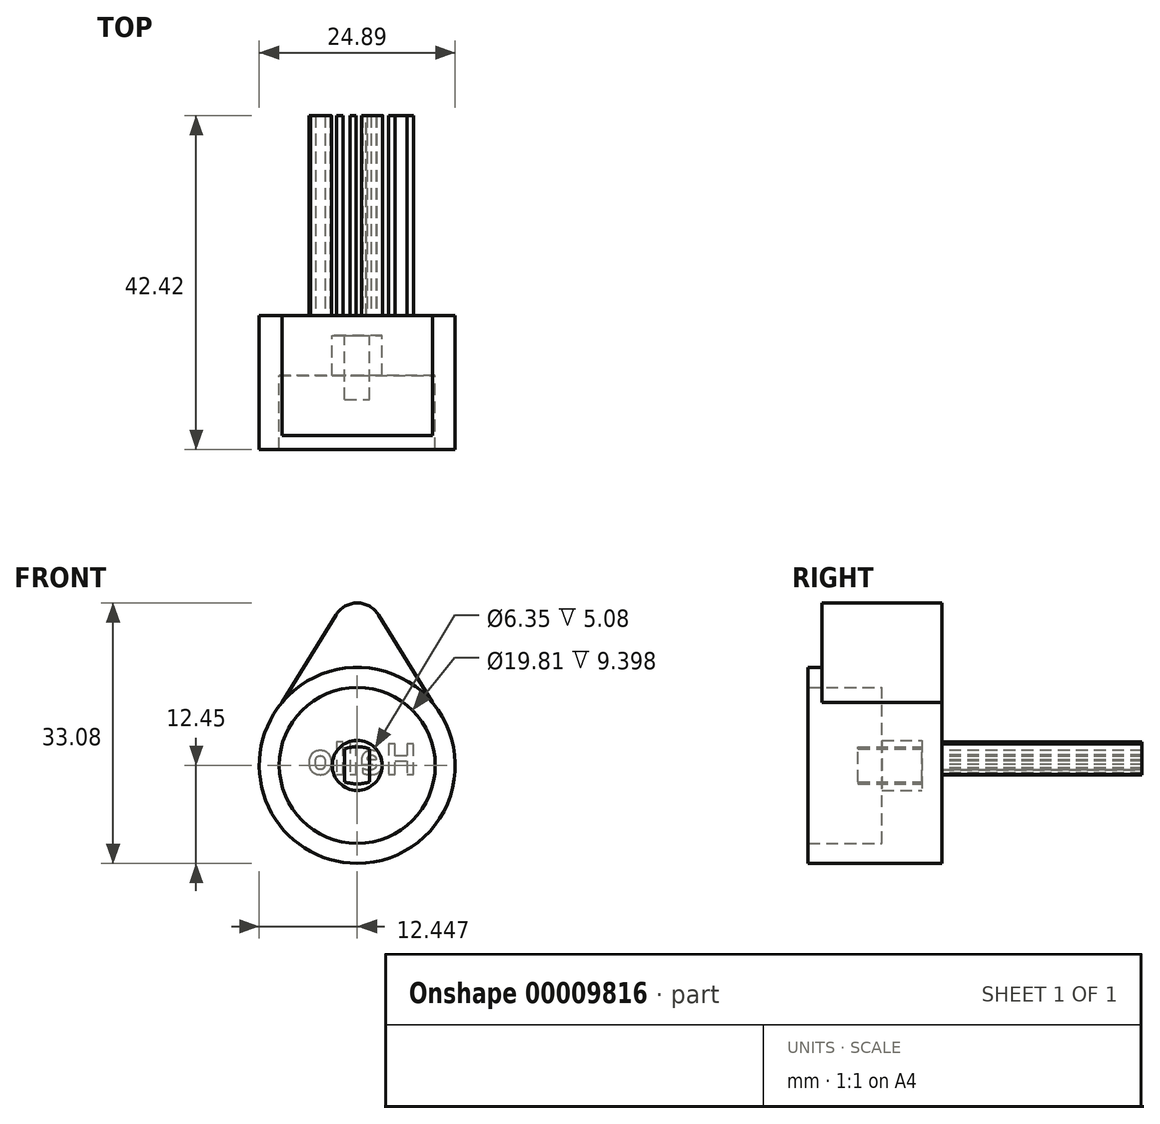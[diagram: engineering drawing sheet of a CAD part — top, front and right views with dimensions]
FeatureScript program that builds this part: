
annotation { "Feature Type Name" : "Feature", "Feature Type Description" : "" }
export const myFeature = defineFeature(function(context is Context, id is Id, definition is map)
    precondition{}
    {
        {
            var Q0;
            Q0=qCreatedBy(makeId("Front.planeOp"),FACE);
            var sketch = newSketch(context, id + "F0", { "sketchPlane" : qUnion([Q0])});
            skArc(sketch, "E0.0.MirrorCS", {"start": v(3.18, 0.25) * mm, "mid": v(1.59, 0) * mm, "end": v(0, 0.25) * mm});
            skLineSegment(sketch, "E1", {"start": v(0, 0.25) * mm, "end": v(0, 4.45) * mm});
            skLineSegment(sketch, "E2", {"start": v(3.18, 0.25) * mm, "end": v(3.18, 4.45) * mm});
            skArc(sketch, "E3.0.MirrorCS", {"start": v(3.18, 4.45) * mm, "mid": v(1.59, 4.7) * mm, "end": v(0, 4.45) * mm});
            skCircle(sketch, "E4", {"center": v(1.59, 2.35) * mm, "radius": 12.45 * mm});
            skPoint(sketch, "E5.0.MirrorCS.end.orphan", {"position": v(1.59, 4.45) * mm});
            skPoint(sketch, "E6.orphan", {"position": v(1.59, 4.7) * mm});
            skPoint(sketch, "E7.orphan", {"position": v(0, 2.35) * mm});
            skPoint(sketch, "E8.end.orphan", {"position": v(3.17, 2.35) * mm});
            skPoint(sketch, "E9.end.orphan", {"position": v(1.59, 0) * mm});
            skPoint(sketch, "E9.start.orphan", {"position": v(1.59, 0.25) * mm});
            skLineSegment(sketch, "E10.0", {"start": v(-2.54, -1.33) * mm, "end": v(-2.54, 6.03) * mm});
            skArc(sketch, "E10.1", {"start": v(5.72, -1.33) * mm, "mid": v(1.59, -2.54) * mm, "end": v(-2.54, -1.33) * mm});
            skLineSegment(sketch, "E10.2", {"start": v(5.72, -1.33) * mm, "end": v(5.72, 6.03) * mm});
            skArc(sketch, "E10.3", {"start": v(5.72, 6.03) * mm, "mid": v(1.59, 7.24) * mm, "end": v(-2.54, 6.03) * mm});
            skCircle(sketch, "E11", {"center": v(1.59, 2.35) * mm, "radius": 9.9 * mm});
            skSolve(sketch);
        }
        {
            var Q0;
            Q0=makeQuery(id+"F0.imprint","IMPRINT",FACE,{"disambiguationData":[TD([[makeQuery(id+"F0.imprint","IMPRINT",EDGE,{"derivedFrom":sQuery(id+"F0.wireOp",EDGE,"E4")}),1.0]])]});
            var Q1;
            Q1=makeQuery(id+"F0.imprint","IMPRINT",FACE,{"disambiguationData":[TD([[makeQuery(id+"F0.imprint","IMPRINT",EDGE,{"derivedFrom":sQuery(id+"F0.wireOp",EDGE,"E0.0.MirrorCS")}),1.0]])]});
            extrude(context, id + "F1", {"entities" : qUnion([Q0, Q1]), "depth" : 8.13 * mm});
        }
        {
            var Q0;
            Q0=makeQuery(id+"F1.opExtrude","CAP_FACE",FACE,{"disambiguationData":[OSD([sQuery(id+"F0.wireOp",EDGE,"E4"),sQuery(id+"F0.wireOp",EDGE,"E11")])],"isStart":false});
            var sketch = newSketch(context, id + "F2", { "sketchPlane" : qUnion([Q0])});
            skCircle(sketch, "E12", {"center": v(1.59, 2.35) * mm, "radius": 9.9 * mm});
            skCircle(sketch, "E13", {"center": v(1.59, 2.35) * mm, "radius": 12.45 * mm});
            skSolve(sketch);
        }
        {
            var Q0;
            Q0=makeQuery(id+"F2.imprint","IMPRINT",FACE,{"disambiguationData":[TD([[makeQuery(id+"F2.imprint","IMPRINT",EDGE,{"derivedFrom":sQuery(id+"F2.wireOp",EDGE,"E12")}),-1.0]])]});
            extrude(context, id + "F3", {"entities" : qUnion([Q0]), "depth" : 6.35 * mm});
        }
        {
            var Q0;
            Q0=makeQuery(id+"F1.opExtrude","CAP_FACE",FACE,{"disambiguationData":[OSD([sQuery(id+"F0.wireOp",EDGE,"E4"),sQuery(id+"F0.wireOp",EDGE,"E11")])],"isStart":true});
            var sketch = newSketch(context, id + "F4", { "sketchPlane" : qUnion([Q0])});
            skCircle(sketch, "E14", {"center": v(-1.59, 2.35) * mm, "radius": 9.9 * mm});
            skCircle(sketch, "E15", {"center": v(-1.59, 2.35) * mm, "radius": 3.18 * mm});
            skSolve(sketch);
        }
        {
            var Q0;
            Q0 = qSketchRegion(id + "F4", true);
            extrude(context, id + "F5", {"entities" : qUnion([Q0]), "oppositeDirection" : true, "depth" : 5.08 * mm});
        }
        {
            var Q0;
            Q0=makeQuery(id+"F1.opExtrude","CAP_FACE",FACE,{"disambiguationData":[OSD([sQuery(id+"F0.wireOp",EDGE,"E4"),sQuery(id+"F0.wireOp",EDGE,"E11")])],"isStart":true});
            var sketch = newSketch(context, id + "F6", { "sketchPlane" : qUnion([Q0])});
            skCircle(sketch, "E16", {"center": v(-1.59, 2.35) * mm, "radius": 12.45 * mm});
            skSolve(sketch);
        }
        {
            var Q0;
            Q0 = qSketchRegion(id + "F6", true);
            extrude(context, id + "F7", {"entities" : qUnion([Q0]), "depth" : 2.54 * mm});
        }
        {
            var Q0;
            Q0=makeQuery(id+"F7.opExtrude","CAP_FACE",FACE,{"disambiguationData":[OSD([sQuery(id+"F6.wireOp",EDGE,"E16")])],"isStart":false});
            var sketch = newSketch(context, id + "F8", { "sketchPlane" : qUnion([Q0])});
            skLineSegment(sketch, "E17", {"start": v(-13.02, 7.27) * mm, "end": v(-4.3, 21.46) * mm});
            skLineSegment(sketch, "E18", {"start": v(1.12, 21.46) * mm, "end": v(9.84, 7.27) * mm});
            skLineSegment(sketch, "E19", {"start": v(9.84, 7.27) * mm, "end": v(3.5, 7.27) * mm});
            skLineSegment(sketch, "E20", {"start": v(-1.59, 7.27) * mm, "end": v(-1.59, 2.35) * mm});
            skLineSegment(sketch, "E21", {"start": v(-1.59, 7.27) * mm, "end": v(-1.59, 12.35) * mm});
            skPoint(sketch, "E22.visualSharp", {"position": v(-1.59, 25.86) * mm});
            skArc(sketch, "E22.filletArc", {"start": v(1.12, 21.46) * mm, "mid": v(-1.59, 22.98) * mm, "end": v(-4.3, 21.46) * mm});
            skArc(sketch, "E23", {"start": v(3.5, 7.27) * mm, "mid": v(-1.59, 12.35) * mm, "end": v(-6.67, 7.27) * mm});
            skLineSegment(sketch, "E24.trimOffspring", {"start": v(-6.67, 7.27) * mm, "end": v(-13.02, 7.27) * mm});
            skLineSegment(sketch, "E25.trimOffspring", {"start": v(-1.59, 22.98) * mm, "end": v(-1.59, 25.86) * mm});
            skSolve(sketch);
        }
        {
            var Q0;
            Q0 = qSketchRegion(id + "F8", true);
            extrude(context, id + "F9", {"entities" : qUnion([Q0]), "operationType" : NewBodyOperationType.ADD, "oppositeDirection" : true, "depth" : 15.24 * mm});
        }
        {
            var Q0;
            Q0=makeQuery(id+"F3.opExtrude","CAP_FACE",FACE,{"disambiguationData":[OSD([sQuery(id+"F2.wireOp",EDGE,"E12"),sQuery(id+"F2.wireOp",EDGE,"E13")])],"isStart":false});
            var sketch = newSketch(context, id + "F10", { "sketchPlane" : qUnion([Q0])});
            skSolve(sketch);
        }
        {
            var Q0;
            Q0=makeQuery(id+"F10.imprint","IMPRINT",FACE,{"disambiguationData":[TD([[makeQuery(id+"F10.imprint","IMPRINT",EDGE,{"derivedFrom":makeQuery(id+"F3.opExtrude","CAP_EDGE",EDGE,{"disambiguationData":[OSD([sQuery(id+"F2.wireOp",EDGE,"E12")])],"isStart":false})}),-1.0]])]});
            var sketch = newSketch(context, id + "F11", { "sketchPlane" : qUnion([Q0])});
            skCircle(sketch, "E26", {"center": v(1.59, 2.35) * mm, "radius": 9.9 * mm});
            skCircle(sketch, "E27", {"center": v(1.59, 2.35) * mm, "radius": 6.57 * mm});
            skSolve(sketch);
        }
        {
            var Q0;
            Q0 = qSketchRegion(id + "F11", true);
            var Q1;
            Q1=makeQuery(id+"F5.opExtrude","CAP_FACE",FACE,{"disambiguationData":[OSD([sQuery(id+"F4.wireOp",EDGE,"E14"),sQuery(id+"F4.wireOp",EDGE,"E15")])],"isStart":false});
            extrude(context, id + "F12", {"entities" : qUnion([Q0]), "operationType" : NewBodyOperationType.REMOVE, "endBound" : BoundingType.UP_TO_SURFACE, "oppositeDirection" : true, "endBoundEntityFace" : qUnion([Q1]), "depth" : 25.4 * mm});
        }
        {
            var Q0;
            Q0=makeQuery(id+"F9.boolean.opBoolean","MERGE",FACE,{"derivedFrom":[makeQuery(id+"F7.opExtrude","CAP_FACE",FACE,{"disambiguationData":[OSD([sQuery(id+"F6.wireOp",EDGE,"E16")])],"isStart":false}),makeQuery(id+"F9.opExtrude","CAP_FACE",FACE,{"disambiguationData":[OSD([sQuery(id+"F8.wireOp",EDGE,"E17"),sQuery(id+"F8.wireOp",EDGE,"E18"),sQuery(id+"F8.wireOp",EDGE,"E19"),sQuery(id+"F8.wireOp",EDGE,"E22.filletArc"),sQuery(id+"F8.wireOp",EDGE,"E23"),sQuery(id+"F8.wireOp",EDGE,"E24.trimOffspring")])],"isStart":true})]});
            var sketch = newSketch(context, id + "F13", { "sketchPlane" : qUnion([Q0])});
            skText(sketch, "E28", { "text": "Hello", "fontName": "OpenSans-Bold.ttf"});
            const initialGuessF13  = {"E28": [-0.00922, 0.00122, 1, 0, 0.0039]};
            skSetInitialGuess(sketch, initialGuessF13);
            skSolve(sketch);
        }
        {
            var Q0;
            Q0=makeQuery(id+"F13.imprint","IMPRINT",FACE,{"disambiguationData":[TD([[makeQuery(id+"F13.imprint","IMPRINT",EDGE,{"derivedFrom":sQuery(id+"F13.wireOp",EDGE,"E28.sketch_text.stroke-32")}),-1.0]])]});
            var Q1;
            Q1=makeQuery(id+"F13.imprint","IMPRINT",FACE,{"disambiguationData":[TD([[makeQuery(id+"F13.imprint","IMPRINT",EDGE,{"derivedFrom":sQuery(id+"F13.wireOp",EDGE,"E28.sketch_text.stroke-36")}),-1.0]])]});
            var Q2;
            Q2=makeQuery(id+"F13.imprint","IMPRINT",FACE,{"disambiguationData":[TD([[makeQuery(id+"F13.imprint","IMPRINT",EDGE,{"derivedFrom":sQuery(id+"F13.wireOp",EDGE,"E28.sketch_text.stroke-12")}),-1.0]])]});
            var Q3;
            Q3=makeQuery(id+"F13.imprint","IMPRINT",FACE,{"disambiguationData":[TD([[makeQuery(id+"F13.imprint","IMPRINT",EDGE,{"derivedFrom":sQuery(id+"F13.wireOp",EDGE,"E28.sketch_text.stroke-40")}),-1.0]])]});
            var Q4;
            Q4=makeQuery(id+"F13.imprint","IMPRINT",FACE,{"disambiguationData":[TD([[makeQuery(id+"F13.imprint","IMPRINT",EDGE,{"derivedFrom":sQuery(id+"F13.wireOp",EDGE,"E28.sketch_text.stroke-0")}),-1.0]])]});
            extrude(context, id + "F14", {"entities" : qUnion([Q0, Q1, Q2, Q3, Q4]), "operationType" : NewBodyOperationType.ADD, "depth" : 25.4 * mm});
        }
    });
